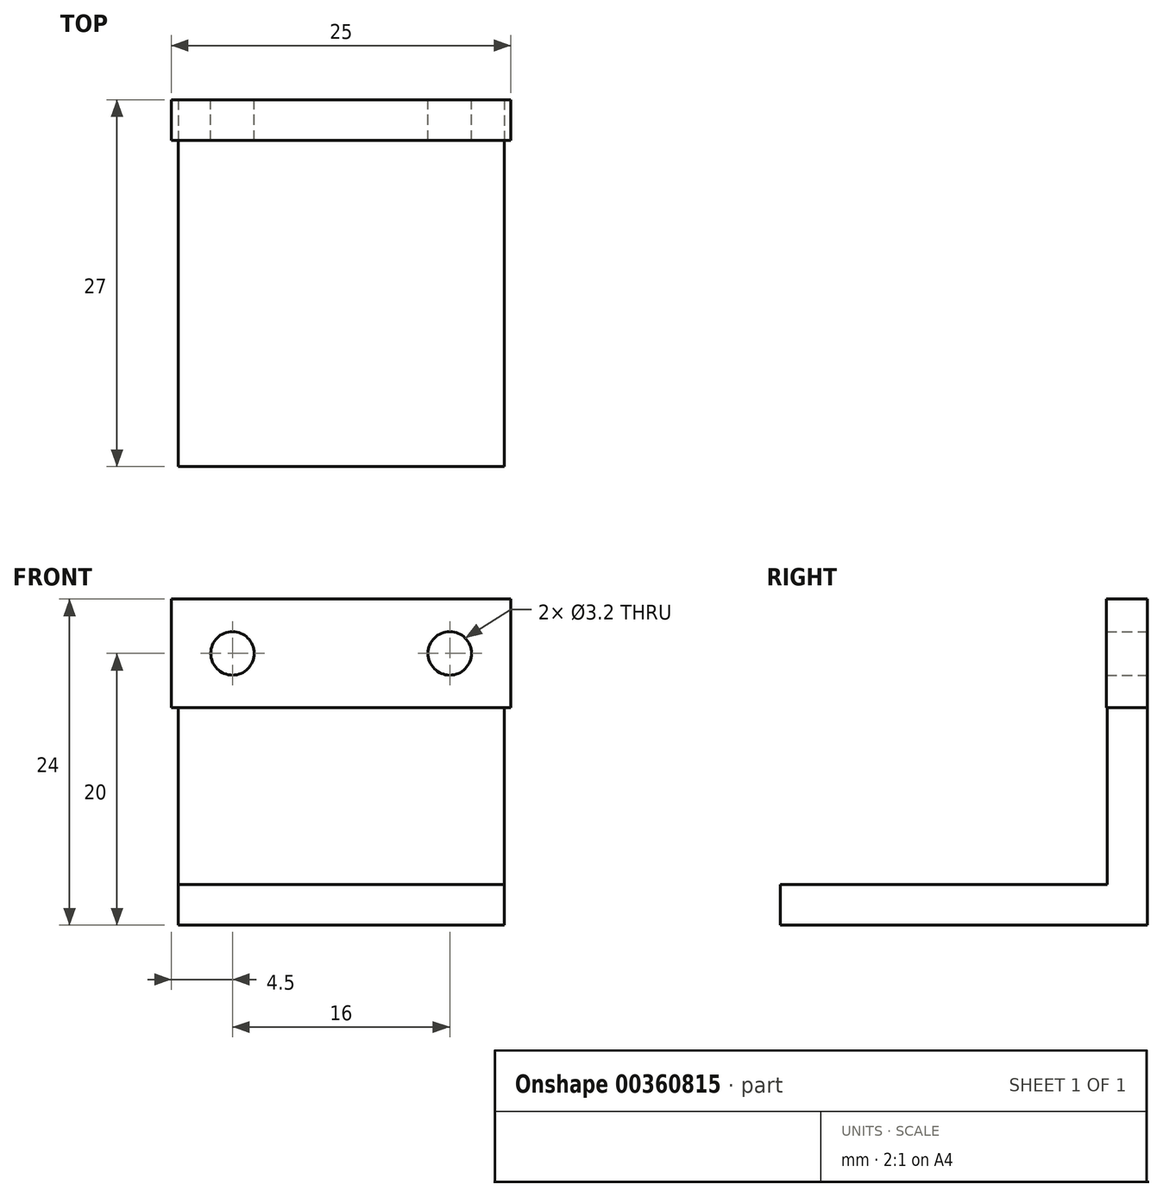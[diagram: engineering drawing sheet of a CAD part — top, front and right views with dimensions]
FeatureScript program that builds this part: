
annotation { "Feature Type Name" : "Feature", "Feature Type Description" : "" }
export const myFeature = defineFeature(function(context is Context, id is Id, definition is map)
    precondition{}
    {
        {
            var Q0;
            Q0=qCreatedBy(makeId("Front.planeOp"),FACE);
            var sketch = newSketch(context, id + "F0", { "sketchPlane" : qUnion([Q0])});
            skLineSegment(sketch, "E0.bottom", {"start": v(12.5, 4) * mm, "end": v(-12.5, 4) * mm});
            skLineSegment(sketch, "E0.top", {"start": v(12.5, -4) * mm, "end": v(-12.5, -4) * mm});
            skLineSegment(sketch, "E0.left", {"start": v(12.5, 4) * mm, "end": v(12.5, -4) * mm});
            skLineSegment(sketch, "E0.right", {"start": v(-12.5, 4) * mm, "end": v(-12.5, -4) * mm});
            skPoint(sketch, "E0.middle", {"position": v(0, 0) * mm});
            skCircle(sketch, "E1", {"center": v(8, 0) * mm, "radius": 1.6 * mm});
            skCircle(sketch, "E2", {"center": v(-8, 0) * mm, "radius": 1.6 * mm});
            skSolve(sketch);
        }
        {
            var Q0;
            Q0=makeQuery(id+"F0.imprint","IMPRINT",FACE,{"disambiguationData":[TD([[makeQuery(id+"F0.imprint","IMPRINT",EDGE,{"derivedFrom":sQuery(id+"F0.wireOp",EDGE,"E0.bottom")}),1.0]])]});
            extrude(context, id + "F1", {"entities" : qUnion([Q0]), "depth" : 3 * mm});
        }
        {
            var Q0;
            Q0=qCreatedBy(makeId("Right.planeOp"),FACE);
            var sketch = newSketch(context, id + "F2", { "sketchPlane" : qUnion([Q0])});
            skLineSegment(sketch, "E3.top", {"start": v(0, -20) * mm, "end": v(-2.95, -20) * mm});
            skLineSegment(sketch, "E3.right", {"start": v(-2.95, -3.97) * mm, "end": v(-2.95, -20) * mm});
            skLineSegment(sketch, "E4.bottom", {"start": v(0, -20) * mm, "end": v(-27, -20) * mm});
            skLineSegment(sketch, "E4.top", {"start": v(0, -17) * mm, "end": v(-27, -17) * mm});
            skLineSegment(sketch, "E4.left", {"start": v(0, -20) * mm, "end": v(0, -17) * mm});
            skLineSegment(sketch, "E4.right", {"start": v(-27, -20) * mm, "end": v(-27, -17) * mm});
            skLineSegment(sketch, "E5", {"start": v(-2.95, -3.97) * mm, "end": v(0, -3.97) * mm});
            skLineSegment(sketch, "E6", {"start": v(0, -3.97) * mm, "end": v(0, -17) * mm});
            skSolve(sketch);
        }
        {
            var Q0;
            Q0 = qSketchRegion(id + "F2", true);
            extrude(context, id + "F3", {"entities" : qUnion([Q0]), "operationType" : NewBodyOperationType.ADD, "depth" : 12 * mm, "hasSecondDirection" : true, "secondDirectionOppositeDirection" : true, "secondDirectionDepth" : 12 * mm});
        }
    });
